FCSTD DOCUMENT  (FreeCAD 0.20R29410 (Git))
Label: TxtDraft
License: All rights reserved
LicenseURL: http://en.wikipedia.org/wiki/All_rights_reserved
objects: Part::FeaturePython×2, App::DocumentObjectGroup×2, Part::Part2DObjectPython×1
note: 3 computed .brp shape members not serialized (recipe doc carries the construction recipe); baked Part::Feature solids carry a one-line shape summary decoded from their .brp

FEATURE [Part::Part2DObjectPython] ShapeString  # Draft 2D object (typed FeaturePython)
  FontFile = <path>
  MakeFace = true
  Placement = pos=(-12.66,-4.33,0) rot=(0,0,1;0rad)
  Size = 10
  String = ABC
  Tracking = 0
FEATURE [Part::FeaturePython] NPointsPoint_P  # WARN: FeaturePython — macro-defined, semantics opaque (R4)
  Parametric = 0
  Points = -> [ShapeString]
  X = 12.6643
  Y = 0.698925
  Z = 0
FEATURE [Part::FeaturePython] NPointsPoint_P001  # WARN: FeaturePython — macro-defined, semantics opaque (R4)
  Parametric = 0
  Points = -> [ShapeString]
  X = 21.4138
  Y = 4.33294
  Z = 0
FEATURE [App::DocumentObjectGroup] WorkPoints_P
  Group = -> [NPointsPoint_P,NPointsPoint_P001]
FEATURE [App::DocumentObjectGroup] WorkFeatures
  Group = -> [WorkPoints_P]
note: 1 file-system path scrubbed to <path> (originals preserved in the JSON sidecar)
